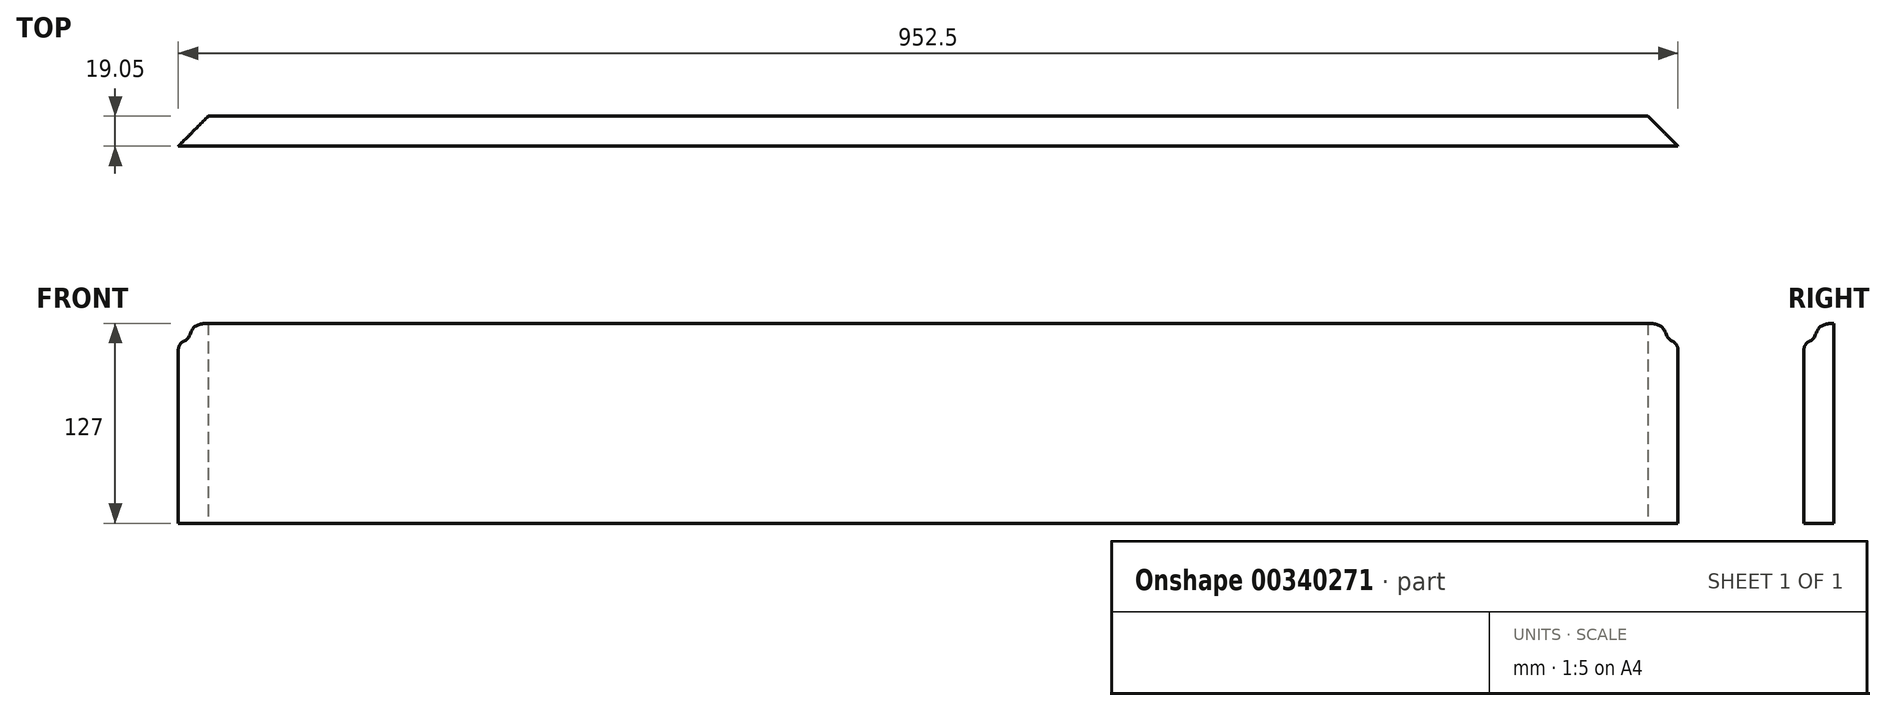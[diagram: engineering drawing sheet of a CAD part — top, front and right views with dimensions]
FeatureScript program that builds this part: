
annotation { "Feature Type Name" : "Feature", "Feature Type Description" : "" }
export const myFeature = defineFeature(function(context is Context, id is Id, definition is map)
    precondition{}
    {
        {
            var Q0;
            Q0=qCreatedBy(makeId("Front.planeOp"),FACE);
            var sketch = newSketch(context, id + "F0", { "sketchPlane" : qUnion([Q0])});
            skLineSegment(sketch, "E0.bottom", {"start": v(476.25, -63.5) * mm, "end": v(-476.25, -63.5) * mm});
            skLineSegment(sketch, "E0.top", {"start": v(476.25, 63.5) * mm, "end": v(-476.25, 63.5) * mm});
            skLineSegment(sketch, "E0.left", {"start": v(476.25, -63.5) * mm, "end": v(476.25, 63.5) * mm});
            skLineSegment(sketch, "E0.right", {"start": v(-476.25, -63.5) * mm, "end": v(-476.25, 63.5) * mm});
            skPoint(sketch, "E0.middle", {"position": v(0, 0) * mm});
            skSolve(sketch);
        }
        {
            var Q0;
            Q0 = qSketchRegion(id + "F0", true);
            extrude(context, id + "F1", {"entities" : qUnion([Q0]), "depth" : 19.05 * mm});
        }
        {
            var Q0;
            Q0=makeQuery(id+"F1.opExtrude","SWEPT_FACE",FACE,{"disambiguationData":[OSD([sQuery(id+"F0.wireOp",EDGE,"E0.left")])]});
            var sketch = newSketch(context, id + "F2", { "sketchPlane" : qUnion([Q0])});
            skFitSpline(sketch, "E1", {"points": [v(0, 63.5) * mm, v(-19.05, 51.53) * mm], "startDerivative": vector(-48.08, 0) * mm, "endDerivative": vector(-35.63, -1.9) * mm});
            skArc(sketch, "E2.filletArc", {"start": v(-15.26, 52.32) * mm, "mid": v(-18.02, 49.98) * mm, "end": v(-19.05, 46.5) * mm});
            skLineSegment(sketch, "E3", {"start": v(0, 63.5) * mm, "end": v(-19.05, 63.5) * mm});
            skLineSegment(sketch, "E4", {"start": v(-19.05, 63.5) * mm, "end": v(-19.05, 46.5) * mm});
            skSolve(sketch);
        }
        {
            var Q0;
            Q0 = qSketchRegion(id + "F2", true);
            extrude(context, id + "F3", {"entities" : qUnion([Q0]), "operationType" : NewBodyOperationType.REMOVE, "endBound" : BoundingType.THROUGH_ALL, "oppositeDirection" : true, "depth" : 25.4 * mm});
        }
        {
            var Q0;
            Q0=makeQuery(id+"F1.opExtrude","SWEPT_FACE",FACE,{"disambiguationData":[OSD([sQuery(id+"F0.wireOp",EDGE,"E0.bottom")])]});
            var sketch = newSketch(context, id + "F4", { "sketchPlane" : qUnion([Q0])});
            skLineSegment(sketch, "E5", {"start": v(-476.25, 19.05) * mm, "end": v(-476.25, 0) * mm});
            skLineSegment(sketch, "E6", {"start": v(0, 19.05) * mm, "end": v(0, 0) * mm, "construction": true});
            skLineSegment(sketch, "E7", {"start": v(-476.25, 0) * mm, "end": v(-457.2, 0) * mm});
            skLineSegment(sketch, "E8", {"start": v(-457.2, 0) * mm, "end": v(-476.25, 19.05) * mm});
            skLineSegment(sketch, "E9.MirrorCS", {"start": v(457.2, 0) * mm, "end": v(476.25, 19.05) * mm});
            skLineSegment(sketch, "E10.MirrorCS", {"start": v(476.25, 19.05) * mm, "end": v(476.25, 0) * mm});
            skLineSegment(sketch, "E11.MirrorCS", {"start": v(476.25, 0) * mm, "end": v(457.2, 0) * mm});
            skSolve(sketch);
        }
        {
            var Q0;
            Q0 = qSketchRegion(id + "F4", true);
            extrude(context, id + "F5", {"entities" : qUnion([Q0]), "operationType" : NewBodyOperationType.REMOVE, "endBound" : BoundingType.THROUGH_ALL, "oppositeDirection" : true, "depth" : 25.4 * mm});
        }
    });
